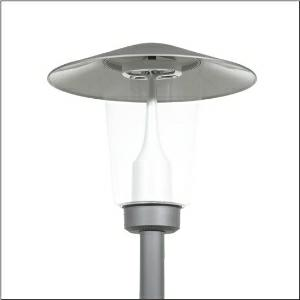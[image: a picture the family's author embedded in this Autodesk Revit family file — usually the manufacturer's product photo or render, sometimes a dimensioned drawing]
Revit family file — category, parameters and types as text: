
# Revit family: pilzleuchte_iq___st1_2a_5xa5235mf14hp_ceaa
name_source: partatom
category: Lighting Fixtures
units: mm (PartAtom-declared; Revit-internal decimal feet)

## family parameters
Cut with Voids When Loaded = No
Host = Face
Light Source = No
Part Type = Normal
Room Calculation Point = No
Round Connector Dimension = Use Diameter
Shared = No

## types (1)
- --- (1 x LED, 4280 lm, 33.6 W, 2700K)
    Apparent Load = 34 VA
    CIE Flux Codes = 23 60 92 98 100
    Color Rendering = 70
    Color Temperature = 2700K
    Default Elevation = 1800 mm
    Description = Mushroom Luminaire iQ, mast luminaire, Module 540 iQ-SR, primary light control with 3 zone facetted reflector, of plastic, silver coated, highly specular, structured, primary optical cover: cover, of PMMA, transparent, light distribution: ST1.2a, light emission: direct distribution, primary light characteristic: asymmetric, installation type: post-top, LED, High Power LED, rated luminous flux: 4.280lm, luminous efficacy: 127lm/W, light colour: 727, colour temperature: 2700K, control gear: iQ Street-Remote, control: pre-setting: logarithmic dimming characteristic, Street-Remote, Auto-Match, Temp-Guard, Lumen-Switch, Night-Set, Smart-Wire, Light-Fading, Desk-Remote (wireless, voltage-free reading and setting of iQ features in the workshop via application-optimized NFC function/RFID function), optimised constant luminous flux control (CLO 2.0), with terminal, 6-pole, max. 2.5mm², mains connection: 230..240V, AC, 50/60Hz, start of lifetime: 34W, end of service life: 36W, reduction: 15W, luminaire housing, upper part, of glass-fibre reinforced polyester, coated, Siteco® metallic grey (DB 702S), diameter: 650mm, height: 586mm, spigot size: d x l = 76 x 70mm (post-top) | with reducer (optional accessory) 60 x 70mm, mounting height: 3..5m, post-top mast mounting element, of diecast aluminium, coated, Siteco® metallic grey (DB 702S), Module 540 iQ-SR, traffic white (RAL 9016), equipment: Power, protection rating (complete): IP65, insulation class (complete): insulation class II (safety insulation), certification: CE, ENEC, VDE, packaging unit: 1 piece

Light Distribution: ST1.2a
    Height = 586 mm
    Lamp = 1 x LED
    Lamp Light Flux = 4280 lm
    Lamp Power = 33.6 W
    Lamp count = 1
    Length = 650 mm
    Luminous efficacy = 127 lm/W
    Manufacturer = Siteco
    ModVariant = No
    Model = 5XA5235MF14HP
    Number of Poles = 1
    OnlyDefault = Yes
    Power Factor = 1
    Product Name = Pilzleuchte iQ | ST1.2a
    Product group = mast luminaire | pylon top
    ProductGroupID = 6100
    Protection Class = Protection class II
    Protection Degree = IP 65
    RLX_Detail_Level = 1
    RLX_Emergency_Light_Flux = 0 lm
    RLX_Emergency_Type = 0
    RLX_Emergency_Type_DB = No
    RlxData = <blob elided: 51469 chars, md5=d66ea057>
    Socket = socket
    Standby Power = 0 W
    System Light Flux = 4280 lm
    System Power = 34 W
    Type Comments = factory setting: luminous flux: 100 % | dim-lin: 254 | 695 mA
    Type Image = l_1006077.jpg
    URL = http://relux.com
    VarID = @adj_152808
    Voltage = 0 V
    Weight = 0.00 kg
    Width = 0 mm  [stored 0 ft]

note: [stored X ft] marks values corroborated as IEEE doubles in the binary element streams (Revit-internal decimal feet)

## geometry (parser evidence)
native form markers: Blend x4, Sweep x12
no freeform markers — native parametric forms only
